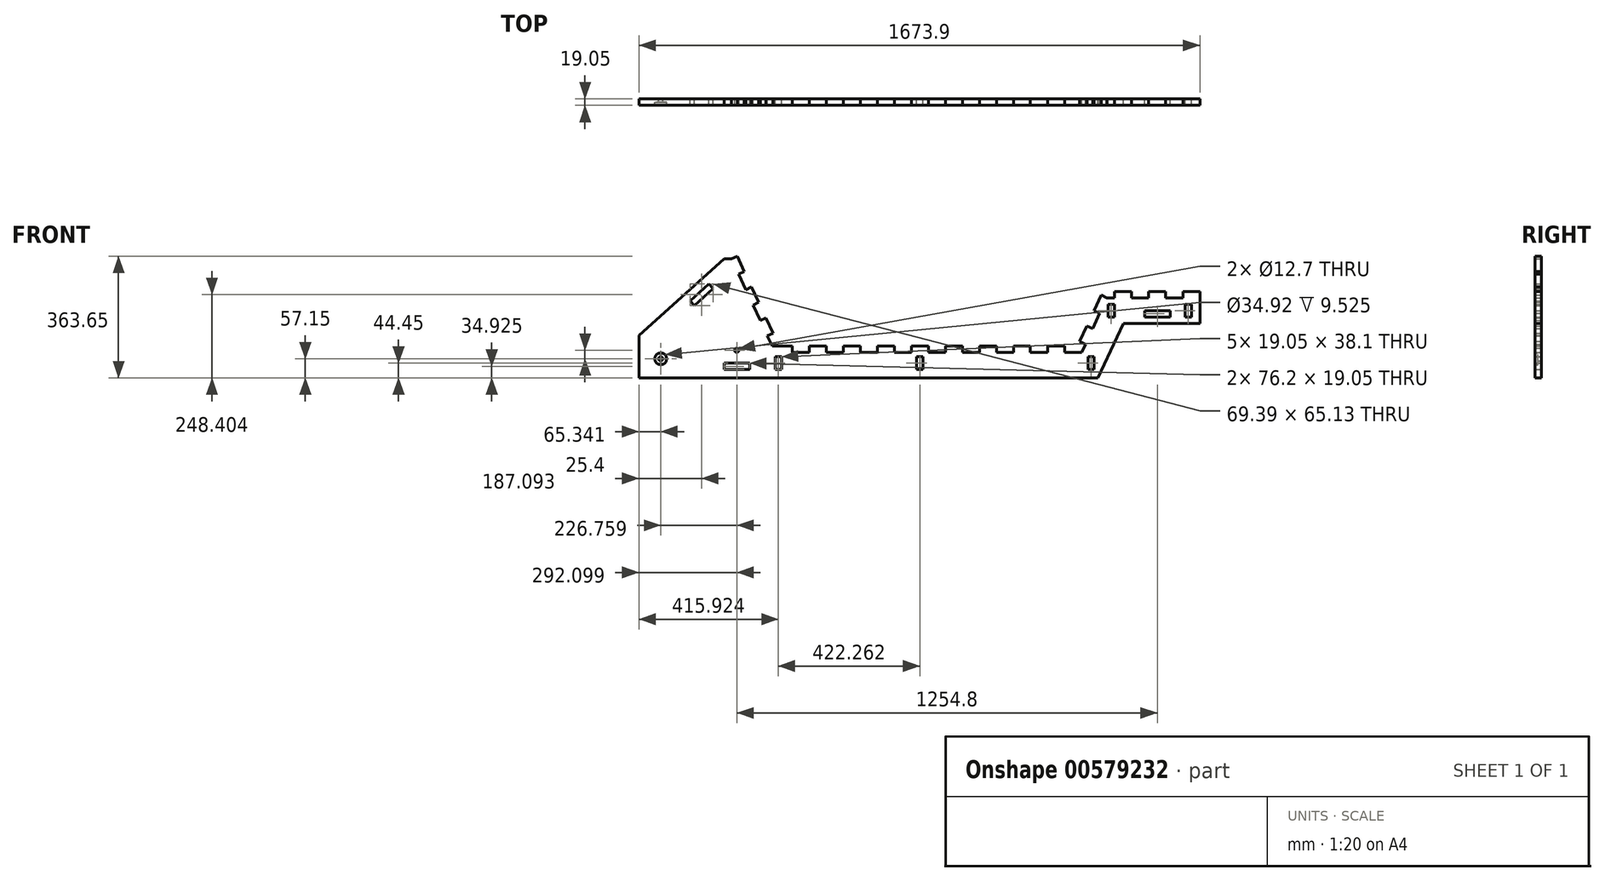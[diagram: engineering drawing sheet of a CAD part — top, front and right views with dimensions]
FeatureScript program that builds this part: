
annotation { "Feature Type Name" : "Feature", "Feature Type Description" : "" }
export const myFeature = defineFeature(function(context is Context, id is Id, definition is map)
    precondition{}
    {
        {
            var Q0;
            Q0=qCreatedBy(makeId("Front.planeOp"),FACE);
            var sketch = newSketch(context, id + "F0", { "sketchPlane" : qUnion([Q0])});
            skLineSegment(sketch, "E0.bottom", {"start": v(-540.23, 76.2) * mm, "end": v(-489.43, 76.2) * mm});
            skLineSegment(sketch, "E0.top", {"start": v(-591.03, 0) * mm, "end": v(342.42, 0) * mm});
            skLineSegment(sketch, "E1", {"start": v(-591.03, 0) * mm, "end": v(-997.43, 0) * mm});
            skLineSegment(sketch, "E2", {"start": v(-721.32, 355.6) * mm, "end": v(-743.43, 355.6) * mm});
            skLineSegment(sketch, "E3", {"start": v(-699.85, 309.56) * mm, "end": v(-678.38, 263.52) * mm});
            skLineSegment(sketch, "E4.MirrorCS", {"start": v(399.33, 239.1) * mm, "end": v(421.44, 239.1) * mm});
            skLineSegment(sketch, "E5", {"start": v(676.47, 239.1) * mm, "end": v(676.47, 162.9) * mm});
            skLineSegment(sketch, "E6", {"start": v(676.47, 162.9) * mm, "end": v(502.2, 162.9) * mm});
            skLineSegment(sketch, "E7", {"start": v(342.42, 0) * mm, "end": v(371.91, 0) * mm});
            skLineSegment(sketch, "E8", {"start": v(392.43, 44) * mm, "end": v(371.91, 0) * mm});
            skLineSegment(sketch, "E9.top", {"start": v(-286.23, 95.25) * mm, "end": v(-235.43, 95.25) * mm});
            skLineSegment(sketch, "E9.left", {"start": v(-286.23, 76.2) * mm, "end": v(-286.23, 95.25) * mm});
            skLineSegment(sketch, "E9.right", {"start": v(-235.43, 76.2) * mm, "end": v(-235.43, 95.25) * mm});
            skLineSegment(sketch, "E10.bottom", {"start": v(-656.9, 217.48) * mm, "end": v(-635.44, 171.44) * mm});
            skLineSegment(sketch, "E10.left", {"start": v(-656.9, 217.48) * mm, "end": v(-639.64, 225.53) * mm});
            skLineSegment(sketch, "E10.right", {"start": v(-635.44, 171.44) * mm, "end": v(-618.18, 179.49) * mm});
            skLineSegment(sketch, "E11.top", {"start": v(-661.11, 271.57) * mm, "end": v(-639.64, 225.53) * mm});
            skLineSegment(sketch, "E11.left", {"start": v(-678.38, 263.52) * mm, "end": v(-661.11, 271.57) * mm});
            skLineSegment(sketch, "E12.left", {"start": v(-699.85, 309.56) * mm, "end": v(-682.58, 317.61) * mm});
            skLineSegment(sketch, "E13.top", {"start": v(-704.05, 363.65) * mm, "end": v(-682.58, 317.61) * mm});
            skLineSegment(sketch, "E13.left", {"start": v(-721.32, 355.6) * mm, "end": v(-704.05, 363.65) * mm});
            skLineSegment(sketch, "E14.top", {"start": v(-618.18, 179.49) * mm, "end": v(-596.7, 133.45) * mm});
            skLineSegment(sketch, "E14.right", {"start": v(-613.97, 125.4) * mm, "end": v(-596.7, 133.45) * mm});
            skLineSegment(sketch, "E15.bottom", {"start": v(-613.97, 125.4) * mm, "end": v(-599.91, 95.25) * mm});
            skLineSegment(sketch, "E16.top", {"start": v(-591.03, 95.25) * mm, "end": v(-540.23, 95.25) * mm});
            skLineSegment(sketch, "E16.right", {"start": v(-540.23, 76.2) * mm, "end": v(-540.23, 95.25) * mm});
            skLineSegment(sketch, "E17.right", {"start": v(-489.43, 76.2) * mm, "end": v(-489.43, 95.25) * mm});
            skLineSegment(sketch, "E18.top", {"start": v(-387.83, 95.25) * mm, "end": v(-337.03, 95.25) * mm});
            skLineSegment(sketch, "E18.left", {"start": v(-387.83, 76.2) * mm, "end": v(-387.83, 95.25) * mm});
            skLineSegment(sketch, "E18.right", {"start": v(-337.03, 76.2) * mm, "end": v(-337.03, 95.25) * mm});
            skLineSegment(sketch, "E19.top", {"start": v(-489.43, 95.25) * mm, "end": v(-438.63, 95.25) * mm});
            skLineSegment(sketch, "E19.right", {"start": v(-438.63, 76.2) * mm, "end": v(-438.63, 95.25) * mm});
            skLineSegment(sketch, "E20.bottom", {"start": v(-337.03, 76.2) * mm, "end": v(-286.23, 76.2) * mm});
            skLineSegment(sketch, "E21.bottom", {"start": v(-438.63, 76.2) * mm, "end": v(-387.83, 76.2) * mm});
            skLineSegment(sketch, "E22.bottom", {"start": v(-32.23, 76.2) * mm, "end": v(18.57, 76.2) * mm});
            skLineSegment(sketch, "E22.left", {"start": v(-32.23, 76.2) * mm, "end": v(-32.23, 95.25) * mm});
            skLineSegment(sketch, "E22.right", {"start": v(18.57, 76.2) * mm, "end": v(18.57, 95.25) * mm});
            skLineSegment(sketch, "E23.top", {"start": v(-184.63, 95.25) * mm, "end": v(-133.83, 95.25) * mm});
            skLineSegment(sketch, "E23.left", {"start": v(-184.63, 76.2) * mm, "end": v(-184.63, 95.25) * mm});
            skLineSegment(sketch, "E23.right", {"start": v(-133.83, 76.2) * mm, "end": v(-133.83, 95.25) * mm});
            skLineSegment(sketch, "E24.top", {"start": v(18.57, 95.25) * mm, "end": v(69.37, 95.25) * mm});
            skLineSegment(sketch, "E24.right", {"start": v(69.37, 76.2) * mm, "end": v(69.37, 95.25) * mm});
            skLineSegment(sketch, "E25.bottom", {"start": v(-133.83, 76.2) * mm, "end": v(-83.03, 76.2) * mm});
            skLineSegment(sketch, "E25.right", {"start": v(-83.03, 76.2) * mm, "end": v(-83.03, 95.25) * mm});
            skLineSegment(sketch, "E26.top", {"start": v(-83.03, 95.25) * mm, "end": v(-32.23, 95.25) * mm});
            skLineSegment(sketch, "E27.bottom", {"start": v(-235.43, 76.2) * mm, "end": v(-184.63, 76.2) * mm});
            skLineSegment(sketch, "E28.bottom", {"start": v(170.97, 76.2) * mm, "end": v(221.77, 76.2) * mm});
            skLineSegment(sketch, "E28.left", {"start": v(170.97, 76.2) * mm, "end": v(170.97, 95.25) * mm});
            skLineSegment(sketch, "E28.right", {"start": v(221.77, 76.2) * mm, "end": v(221.77, 95.25) * mm});
            skLineSegment(sketch, "E29.bottom", {"start": v(69.37, 76.2) * mm, "end": v(120.17, 76.2) * mm});
            skLineSegment(sketch, "E29.right", {"start": v(120.17, 76.2) * mm, "end": v(120.17, 95.25) * mm});
            skLineSegment(sketch, "E30.top", {"start": v(221.77, 95.25) * mm, "end": v(272.57, 95.25) * mm});
            skLineSegment(sketch, "E30.right", {"start": v(272.57, 76.2) * mm, "end": v(272.57, 95.25) * mm});
            skLineSegment(sketch, "E31.top", {"start": v(120.17, 95.25) * mm, "end": v(170.97, 95.25) * mm});
            skLineSegment(sketch, "E32.bottom", {"start": v(272.57, 76.2) * mm, "end": v(323.37, 76.2) * mm});
            skLineSegment(sketch, "E33", {"start": v(-591.03, 95.25) * mm, "end": v(-599.91, 95.25) * mm});
            skLineSegment(sketch, "E34.top", {"start": v(625.67, 258.14) * mm, "end": v(676.47, 258.14) * mm});
            skLineSegment(sketch, "E34.left", {"start": v(625.67, 239.1) * mm, "end": v(625.67, 258.14) * mm});
            skLineSegment(sketch, "E34.right", {"start": v(676.47, 239.1) * mm, "end": v(676.47, 258.14) * mm});
            skLineSegment(sketch, "E35.top", {"start": v(523.04, 258.14) * mm, "end": v(573.84, 258.14) * mm});
            skLineSegment(sketch, "E35.left", {"start": v(523.04, 239.1) * mm, "end": v(523.04, 258.14) * mm});
            skLineSegment(sketch, "E35.right", {"start": v(573.84, 239.1) * mm, "end": v(573.84, 258.14) * mm});
            skLineSegment(sketch, "E36.bottom", {"start": v(573.84, 239.1) * mm, "end": v(625.67, 239.1) * mm});
            skLineSegment(sketch, "E37.bottom", {"start": v(472.24, 239.1) * mm, "end": v(523.04, 239.1) * mm});
            skLineSegment(sketch, "E38.top", {"start": v(421.44, 258.14) * mm, "end": v(472.24, 258.14) * mm});
            skLineSegment(sketch, "E38.left", {"start": v(421.44, 239.1) * mm, "end": v(421.44, 258.14) * mm});
            skLineSegment(sketch, "E38.right", {"start": v(472.24, 239.1) * mm, "end": v(472.24, 258.14) * mm});
            skLineSegment(sketch, "E39.right", {"start": v(382.06, 247.14) * mm, "end": v(399.33, 239.1) * mm});
            skLineSegment(sketch, "E40.bottom", {"start": v(382.06, 247.14) * mm, "end": v(360.6, 201.1) * mm});
            skLineSegment(sketch, "E40.right", {"start": v(360.6, 201.1) * mm, "end": v(377.86, 193.05) * mm});
            skLineSegment(sketch, "E41.top", {"start": v(377.86, 193.05) * mm, "end": v(356.39, 147.01) * mm});
            skLineSegment(sketch, "E41.right", {"start": v(339.12, 155.06) * mm, "end": v(356.39, 147.01) * mm});
            skLineSegment(sketch, "E42.bottom", {"start": v(339.12, 155.06) * mm, "end": v(317.65, 109.02) * mm});
            skLineSegment(sketch, "E42.right", {"start": v(317.65, 109.02) * mm, "end": v(334.92, 100.97) * mm});
            skLineSegment(sketch, "E43.top", {"start": v(334.92, 100.97) * mm, "end": v(324.84, 79.36) * mm});
            skLineSegment(sketch, "E44.trimOffspring", {"start": v(324.84, 79.36) * mm, "end": v(323.37, 76.2) * mm});
            skLineSegment(sketch, "E45.bottom", {"start": v(-591.03, 25.4) * mm, "end": v(-571.98, 25.4) * mm});
            skLineSegment(sketch, "E45.top", {"start": v(-591.03, 63.5) * mm, "end": v(-571.98, 63.5) * mm});
            skLineSegment(sketch, "E45.left", {"start": v(-591.03, 25.4) * mm, "end": v(-591.03, 63.5) * mm});
            skLineSegment(sketch, "E45.right", {"start": v(-571.98, 25.4) * mm, "end": v(-571.98, 63.5) * mm});
            skLineSegment(sketch, "E46.bottom", {"start": v(-168.77, 25.4) * mm, "end": v(-149.72, 25.4) * mm});
            skLineSegment(sketch, "E46.top", {"start": v(-168.77, 63.5) * mm, "end": v(-149.72, 63.5) * mm});
            skLineSegment(sketch, "E46.left", {"start": v(-168.77, 25.4) * mm, "end": v(-168.77, 63.5) * mm});
            skLineSegment(sketch, "E46.right", {"start": v(-149.72, 25.4) * mm, "end": v(-149.72, 63.5) * mm});
            skLineSegment(sketch, "E47.bottom", {"start": v(342.42, 25.4) * mm, "end": v(361.47, 25.4) * mm});
            skLineSegment(sketch, "E47.top", {"start": v(342.42, 63.5) * mm, "end": v(361.47, 63.5) * mm});
            skLineSegment(sketch, "E47.left", {"start": v(342.42, 25.4) * mm, "end": v(342.42, 63.5) * mm});
            skLineSegment(sketch, "E47.right", {"start": v(361.47, 25.4) * mm, "end": v(361.47, 63.5) * mm});
            skLineSegment(sketch, "E48.bottom", {"start": v(632.02, 181.94) * mm, "end": v(651.07, 181.94) * mm});
            skLineSegment(sketch, "E48.top", {"start": v(632.02, 220.04) * mm, "end": v(651.07, 220.04) * mm});
            skLineSegment(sketch, "E48.left", {"start": v(632.02, 181.94) * mm, "end": v(632.02, 220.04) * mm});
            skLineSegment(sketch, "E48.right", {"start": v(651.07, 181.94) * mm, "end": v(651.07, 220.04) * mm});
            skLineSegment(sketch, "E49.bottom", {"start": v(402.4, 181.94) * mm, "end": v(421.44, 181.94) * mm});
            skLineSegment(sketch, "E49.top", {"start": v(402.4, 220.04) * mm, "end": v(421.44, 220.04) * mm});
            skLineSegment(sketch, "E49.left", {"start": v(402.4, 181.94) * mm, "end": v(402.4, 220.04) * mm});
            skLineSegment(sketch, "E49.right", {"start": v(421.44, 181.94) * mm, "end": v(421.44, 220.04) * mm});
            skCircle(sketch, "E50", {"center": v(-932.09, 57.15) * mm, "radius": 6.35 * mm});
            skCircle(sketch, "E51", {"center": v(-932.09, 57.15) * mm, "radius": 17.46 * mm});
            skLineSegment(sketch, "E52", {"start": v(502.2, 162.9) * mm, "end": v(447.87, 162.9) * mm});
            skLineSegment(sketch, "E53", {"start": v(392.43, 44) * mm, "end": v(447.87, 162.9) * mm});
            skCircle(sketch, "E54", {"center": v(-705.33, 82.55) * mm, "radius": 6.35 * mm});
            skLineSegment(sketch, "E55.bottom", {"start": v(-743.43, 44.45) * mm, "end": v(-667.23, 44.45) * mm});
            skLineSegment(sketch, "E55.top", {"start": v(-743.43, 25.4) * mm, "end": v(-667.23, 25.4) * mm});
            skLineSegment(sketch, "E55.left", {"start": v(-743.43, 44.45) * mm, "end": v(-743.43, 25.4) * mm});
            skLineSegment(sketch, "E55.right", {"start": v(-667.23, 44.45) * mm, "end": v(-667.23, 25.4) * mm});
            skLineSegment(sketch, "E56.bottom", {"start": v(511.37, 201) * mm, "end": v(587.57, 201) * mm});
            skLineSegment(sketch, "E56.top", {"start": v(511.37, 181.94) * mm, "end": v(587.57, 181.94) * mm});
            skLineSegment(sketch, "E56.left", {"start": v(511.37, 201) * mm, "end": v(511.37, 181.94) * mm});
            skLineSegment(sketch, "E56.right", {"start": v(587.57, 201) * mm, "end": v(587.57, 181.94) * mm});
            skLineSegment(sketch, "E57", {"start": v(-997.43, 0) * mm, "end": v(-997.43, 127) * mm});
            skLineSegment(sketch, "E58", {"start": v(-997.43, 127) * mm, "end": v(-743.43, 355.6) * mm});
            skLineSegment(sketch, "E59.bottom", {"start": v(-845.03, 230) * mm, "end": v(-788.39, 280.97) * mm});
            skLineSegment(sketch, "E59.top", {"start": v(-832.29, 215.84) * mm, "end": v(-775.64, 266.8) * mm});
            skLineSegment(sketch, "E59.right", {"start": v(-788.39, 280.97) * mm, "end": v(-775.64, 266.8) * mm});
            skLineSegment(sketch, "E60", {"start": v(-845.03, 230) * mm, "end": v(-832.29, 215.84) * mm});
            skSolve(sketch);
        }
        {
            var Q0;
            Q0=makeQuery(id+"F0.imprint","IMPRINT",FACE,{"disambiguationData":[TD([[makeQuery(id+"F0.imprint","IMPRINT",EDGE,{"derivedFrom":sQuery(id+"F0.wireOp",EDGE,"E0.top")}),1.0]])]});
            extrude(context, id + "F1", {"entities" : qUnion([Q0]), "depth" : 19.05 * mm, "offsetDistance" : 25.4 * mm});
        }
        {
            var Q0;
            Q0=makeQuery(id+"F0.imprint","IMPRINT",FACE,{"disambiguationData":[TD([[makeQuery(id+"F0.imprint","IMPRINT",EDGE,{"derivedFrom":sQuery(id+"F0.wireOp",EDGE,"E50")}),-1.0]])]});
            extrude(context, id + "F2", {"entities" : qUnion([Q0]), "operationType" : NewBodyOperationType.ADD, "depth" : 9.52 * mm, "offsetDistance" : 25.4 * mm});
        }
    });
